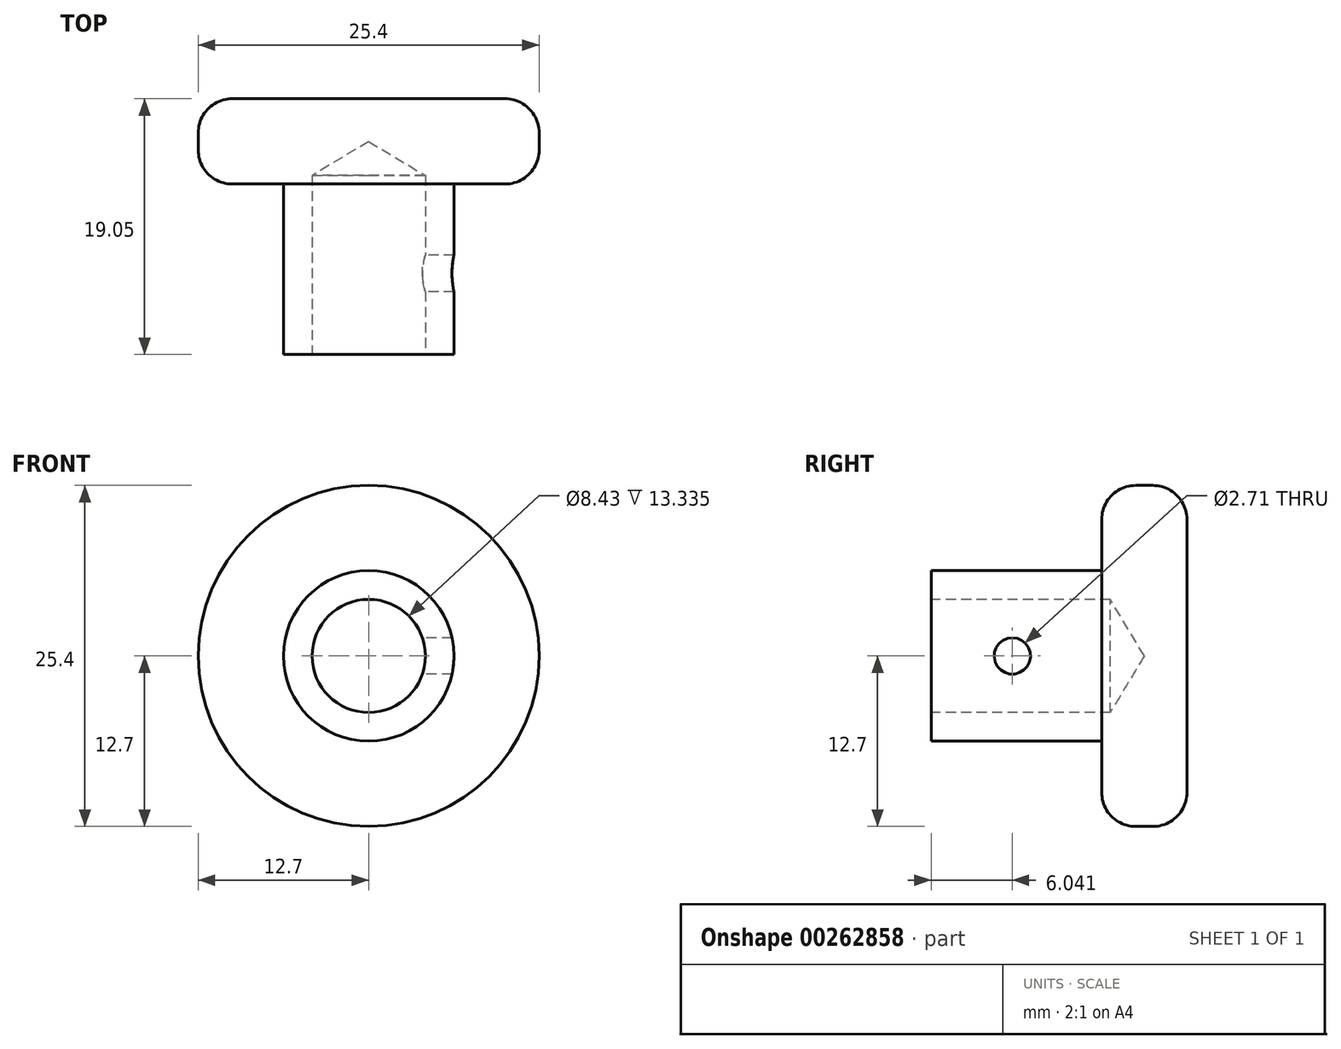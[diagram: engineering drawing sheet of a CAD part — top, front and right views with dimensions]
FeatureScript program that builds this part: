
annotation { "Feature Type Name" : "Feature", "Feature Type Description" : "" }
export const myFeature = defineFeature(function(context is Context, id is Id, definition is map)
    precondition{}
    {
        {
            var Q0;
            Q0=qCreatedBy(makeId("Front.planeOp"),FACE);
            var sketch = newSketch(context, id + "F0", { "sketchPlane" : qUnion([Q0])});
            skCircle(sketch, "E0", {"center": v(0, 0) * mm, "radius": 12.7 * mm});
            skCircle(sketch, "E1", {"center": v(0, 0) * mm, "radius": 6.35 * mm});
            skSolve(sketch);
        }
        {
            var Q0;
            Q0=makeQuery(id+"F0.imprint","IMPRINT",FACE,{"disambiguationData":[TD([[makeQuery(id+"F0.imprint","IMPRINT",EDGE,{"derivedFrom":sQuery(id+"F0.wireOp",EDGE,"E1")}),1.0]])]});
            extrude(context, id + "F1", {"entities" : qUnion([Q0]), "depth" : 19.05 * mm});
        }
        {
            var Q0;
            Q0=makeQuery(id+"F0.imprint","IMPRINT",FACE,{"disambiguationData":[TD([[makeQuery(id+"F0.imprint","IMPRINT",EDGE,{"derivedFrom":sQuery(id+"F0.wireOp",EDGE,"E0")}),1.0]])]});
            extrude(context, id + "F2", {"entities" : qUnion([Q0]), "operationType" : NewBodyOperationType.ADD, "depth" : 6.35 * mm});
        }
        {
            var Q0;
            Q0=makeQuery(id+"F1.opExtrude","CAP_FACE",FACE,{"disambiguationData":[OSD([sQuery(id+"F0.wireOp",EDGE,"E1")])],"isStart":false});
            var sketch = newSketch(context, id + "F3", { "sketchPlane" : qUnion([Q0])});
            skPoint(sketch, "E2", {"position": v(0, 0) * mm});
            skSolve(sketch);
        }
        {
            var Q0;
            Q0=sQuery(id+"F3.wireOp",VERTEX,"E2");
            var Q1;
            Q1=makeQuery(id+"F1.opExtrude","SWEPT_BODY",BODY,{"disambiguationData":[OSD([sQuery(id+"F0.wireOp",EDGE,"E1")])]});
            hole(context, id + "F4", {"style" : HoleStyle.SIMPLE, "endStyle" : HoleEndStyle.BLIND, "standardTappedOrClearance" : lookupTablePath({ "standard" : "ANSI", "engagement" : "75%", "pitch" : "24 tpi", "size" : "3/8", "type" : "Tapped" }), "standardBlindInLast" : lookupTablePath({ "standard" : "ANSI", "engagement" : "75%", "pitch" : "24 tpi", "size" : "3/8", "type" : "Tapped" }), "holeDiameter" : 8.43 * mm, "showTappedDepth" : true, "holeDepth" : 13.33 * mm, "tappedDepth" : 10.16 * mm, "tapClearance" : 3, "startFromSketch" : true, "locations" : qUnion([Q0]), "scope" : qUnion([Q1]), "majorDiameter" : 9.53 * mm});
        }
        {
            var Q0;
            Q0=qCreatedBy(makeId("Right.planeOp"),FACE);
            var sketch = newSketch(context, id + "F5", { "sketchPlane" : qUnion([Q0])});
            skPoint(sketch, "E3", {"position": v(-13, 0) * mm});
            skSolve(sketch);
        }
        {
            var Q0;
            Q0=makeQuery(id+"F2.opExtrude","CAP_EDGE",EDGE,{"disambiguationData":[OSD([sQuery(id+"F0.wireOp",EDGE,"E0")])],"isStart":false});
            var Q1;
            Q1=makeQuery(id+"F2.opExtrude","CAP_EDGE",EDGE,{"disambiguationData":[OSD([sQuery(id+"F0.wireOp",EDGE,"E0")])],"isStart":true});
            fillet(context, id + "F6", {"entities" : qUnion([Q0, Q1]), "radius" : 2.54 * mm, "tangentPropagation" : true, "allowEdgeOverflow" : false});
        }
        {
            var Q0;
            Q0=sQuery(id+"F5.wireOp",VERTEX,"E3");
            var Q1;
            Q1=makeQuery(id+"F1.opExtrude","SWEPT_BODY",BODY,{"disambiguationData":[OSD([sQuery(id+"F0.wireOp",EDGE,"E1")])]});
            hole(context, id + "F7", {"style" : HoleStyle.SIMPLE, "endStyle" : HoleEndStyle.BLIND, "oppositeDirection" : true, "standardTappedOrClearance" : lookupTablePath({ "standard" : "ANSI", "engagement" : "75%", "pitch" : "32 tpi", "size" : "#6", "type" : "Tapped" }), "standardBlindInLast" : lookupTablePath({ "standard" : "ANSI", "engagement" : "75%", "pitch" : "32 tpi", "size" : "#6", "type" : "Tapped" }), "holeDiameter" : 2.7 * mm, "showTappedDepth" : true, "holeDepth" : 7.62 * mm, "tappedDepth" : 5.24 * mm, "tapClearance" : 3, "locations" : qUnion([Q0]), "scope" : qUnion([Q1]), "majorDiameter" : 3.5 * mm});
        }
    });
